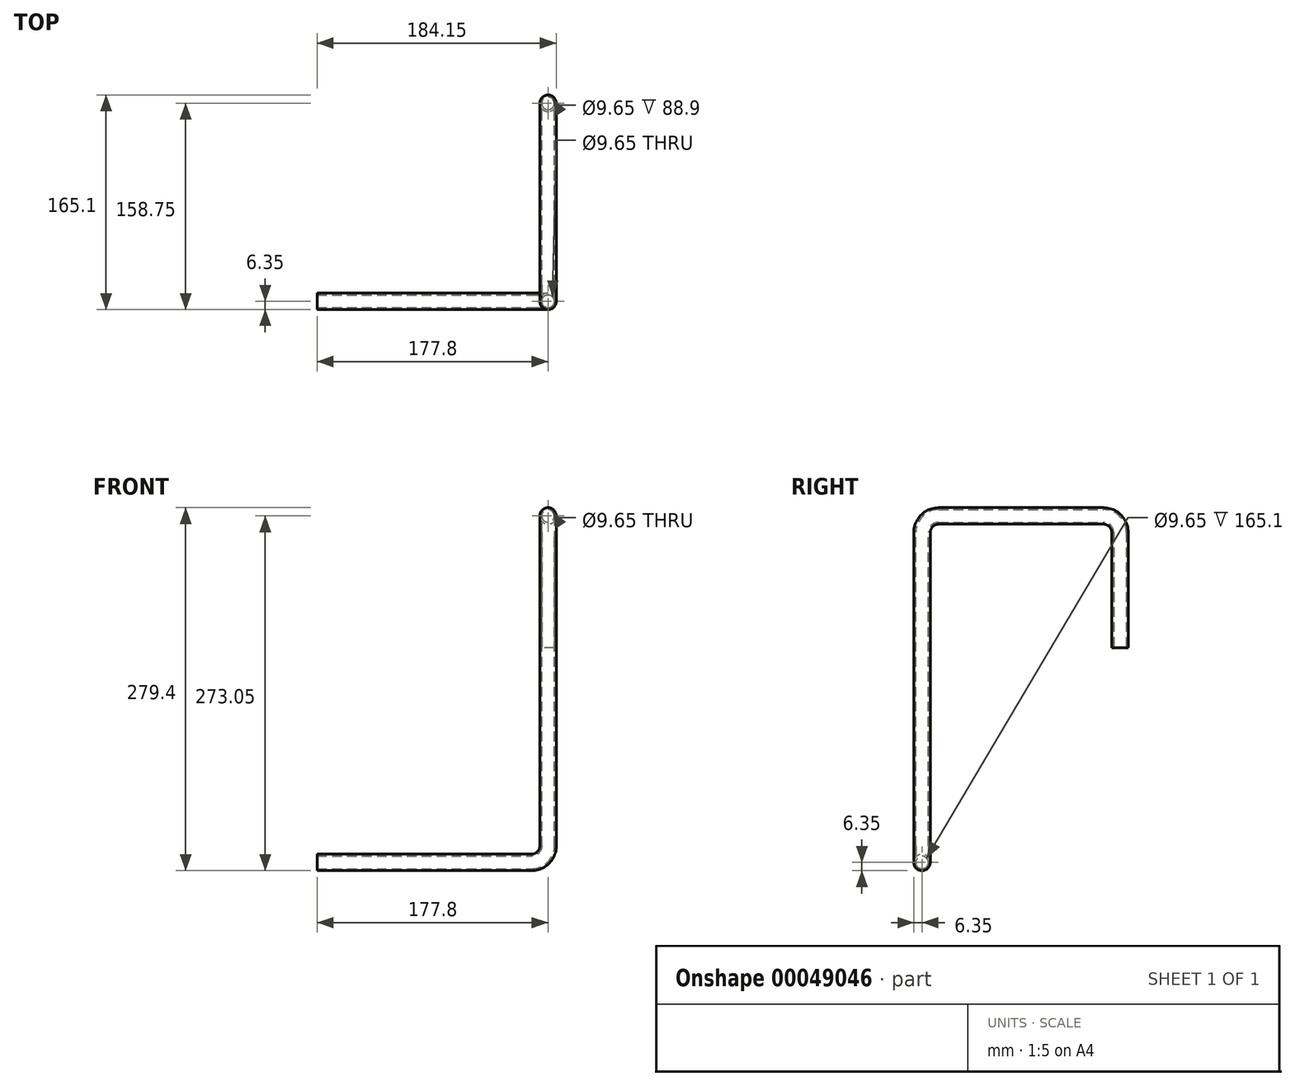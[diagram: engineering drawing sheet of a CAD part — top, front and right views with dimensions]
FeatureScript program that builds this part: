
annotation { "Feature Type Name" : "Feature", "Feature Type Description" : "" }
export const myFeature = defineFeature(function(context is Context, id is Id, definition is map)
    precondition{}
    {
        {
            var Q0;
            Q0=qCreatedBy(makeId("Front.planeOp"),FACE);
            var sketch = newSketch(context, id + "F0", { "sketchPlane" : qUnion([Q0])});
            skLineSegment(sketch, "E0", {"start": v(0, 0) * mm, "end": v(165.1, 0) * mm});
            skLineSegment(sketch, "E1", {"start": v(177.8, 12.7) * mm, "end": v(177.8, 114.11) * mm});
            skPoint(sketch, "E2.visualSharp", {"position": v(177.8, 0) * mm});
            skArc(sketch, "E2.filletArc", {"start": v(165.1, 0) * mm, "mid": v(174.08, 3.72) * mm, "end": v(177.8, 12.7) * mm});
            skSolve(sketch);
        }
        {
            var Q0;
            Q0=sQuery(id+"F0.wireOp",VERTEX,"E1.end");
            var Q1;
            Q1=qCreatedBy(makeId("Right.planeOp"),FACE);
            cPlane(context, id + "F1", {"entities" : qUnion([Q0, Q1]), "cplaneType" : CPlaneType.PLANE_POINT, "offset" : 152.4 * mm, "width" : 152.4 * mm, "height" : 152.4 * mm});
        }
        {
            var Q0;
            Q0=qCreatedBy(id+"F1.planeOp",FACE);
            var sketch = newSketch(context, id + "F2", { "sketchPlane" : qUnion([Q0])});
            skLineSegment(sketch, "E3", {"start": v(12.7, 266.7) * mm, "end": v(139.7, 266.7) * mm});
            skLineSegment(sketch, "E4", {"start": v(152.4, 254) * mm, "end": v(152.4, 165.1) * mm});
            skLineSegment(sketch, "E5", {"start": v(0, 254) * mm, "end": v(0, 114.11) * mm});
            skPoint(sketch, "E6.visualSharp", {"position": v(0, 266.7) * mm});
            skArc(sketch, "E6.filletArc", {"start": v(12.7, 266.7) * mm, "mid": v(3.72, 262.98) * mm, "end": v(0, 254) * mm});
            skPoint(sketch, "E7.visualSharp", {"position": v(152.4, 266.7) * mm});
            skArc(sketch, "E7.filletArc", {"start": v(152.4, 254) * mm, "mid": v(148.68, 262.98) * mm, "end": v(139.7, 266.7) * mm});
            skSolve(sketch);
        }
        {
            var Q0;
            Q0=qCreatedBy(makeId("Right.planeOp"),FACE);
            var sketch = newSketch(context, id + "F3", { "sketchPlane" : qUnion([Q0])});
            skCircle(sketch, "E8", {"center": v(0, 0) * mm, "radius": 6.35 * mm});
            skCircle(sketch, "E9", {"center": v(0, 0) * mm, "radius": 4.83 * mm});
            skSolve(sketch);
        }
        {
            var Q0;
            Q0=makeQuery(id+"F3.imprint","IMPRINT",FACE,{"disambiguationData":[TD([[makeQuery(id+"F3.imprint","IMPRINT",EDGE,{"derivedFrom":sQuery(id+"F3.wireOp",EDGE,"E8")}),1.0]])]});
            var Q1;
            Q1=sQuery(id+"F0.wireOp",EDGE,"E0");
            var Q2;
            Q2=sQuery(id+"F0.wireOp",EDGE,"E2.filletArc");
            var Q3;
            Q3=sQuery(id+"F0.wireOp",EDGE,"E1");
            var Q4;
            Q4=sQuery(id+"F2.wireOp",EDGE,"E5");
            var Q5;
            Q5=sQuery(id+"F2.wireOp",EDGE,"E6.filletArc");
            var Q6;
            Q6=sQuery(id+"F2.wireOp",EDGE,"E3");
            var Q7;
            Q7=sQuery(id+"F2.wireOp",EDGE,"E7.filletArc");
            var Q8;
            Q8=sQuery(id+"F2.wireOp",EDGE,"E4");
            sweep(context, id + "F4", {"profiles" : qUnion([Q0]), "path" : qUnion([Q1, Q2, Q3, Q4, Q5, Q6, Q7, Q8])});
        }
    });
